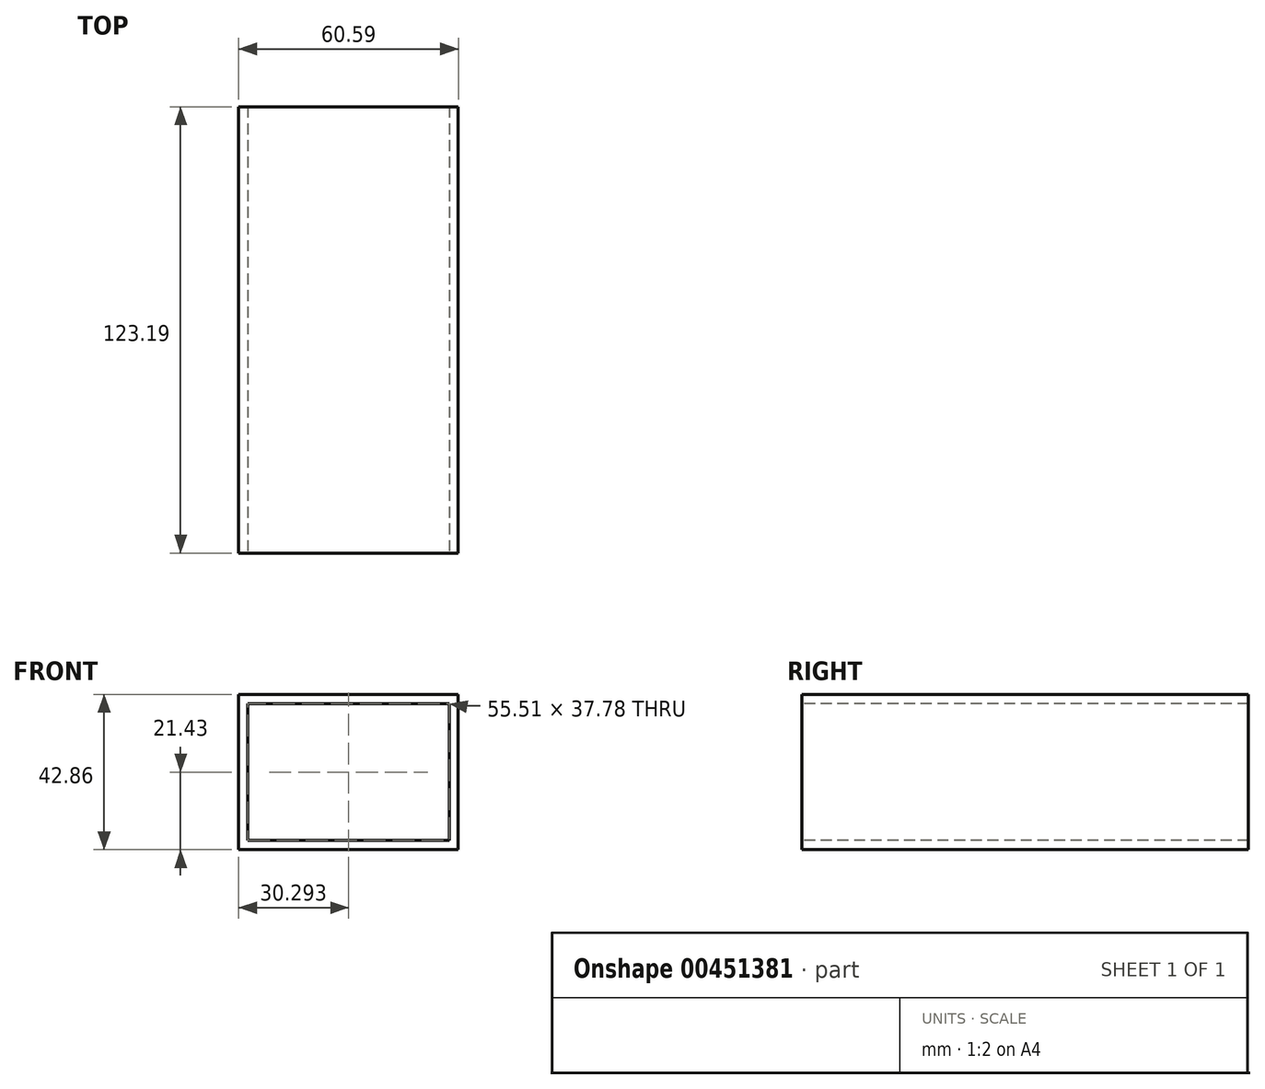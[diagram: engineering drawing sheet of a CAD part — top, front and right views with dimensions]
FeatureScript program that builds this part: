
annotation { "Feature Type Name" : "Feature", "Feature Type Description" : "" }
export const myFeature = defineFeature(function(context is Context, id is Id, definition is map)
    precondition{}
    {
        {
            var Q0;
            Q0=qCreatedBy(makeId("Front.planeOp"),FACE);
            var sketch = newSketch(context, id + "F0", { "sketchPlane" : qUnion([Q0])});
            skLineSegment(sketch, "E0.bottom", {"start": v(-42.43, 32.7) * mm, "end": v(18.16, 32.7) * mm});
            skLineSegment(sketch, "E0.top", {"start": v(-42.43, -10.17) * mm, "end": v(18.16, -10.17) * mm});
            skLineSegment(sketch, "E0.left", {"start": v(-42.43, 32.7) * mm, "end": v(-42.43, -10.17) * mm});
            skLineSegment(sketch, "E0.right", {"start": v(18.16, 32.7) * mm, "end": v(18.16, -10.17) * mm});
            skSolve(sketch);
        }
        {
            var Q0;
            Q0=makeQuery(id+"F0.imprint","IMPRINT",FACE,{"disambiguationData":[TD([[makeQuery(id+"F0.imprint","IMPRINT",EDGE,{"derivedFrom":sQuery(id+"F0.wireOp",EDGE,"E0.bottom")}),-1.0]])]});
            extrude(context, id + "F1", {"entities" : qUnion([Q0]), "oppositeDirection" : true, "depth" : 123.19 * mm});
        }
        {
            var Q0;
            Q0=makeQuery(id+"F1.opExtrude","CAP_FACE",FACE,{"disambiguationData":[OSD([sQuery(id+"F0.wireOp",EDGE,"E0.bottom"),sQuery(id+"F0.wireOp",EDGE,"E0.top"),sQuery(id+"F0.wireOp",EDGE,"E0.left"),sQuery(id+"F0.wireOp",EDGE,"E0.right")])],"isStart":true});
            var Q1;
            Q1=makeQuery(id+"F1.opExtrude","CAP_FACE",FACE,{"disambiguationData":[OSD([sQuery(id+"F0.wireOp",EDGE,"E0.bottom"),sQuery(id+"F0.wireOp",EDGE,"E0.top"),sQuery(id+"F0.wireOp",EDGE,"E0.left"),sQuery(id+"F0.wireOp",EDGE,"E0.right")])],"isStart":false});
            shell(context, id + "F2", {"entities" : qUnion([Q0, Q1]), "thickness" : 2.54 * mm});
        }
    });
